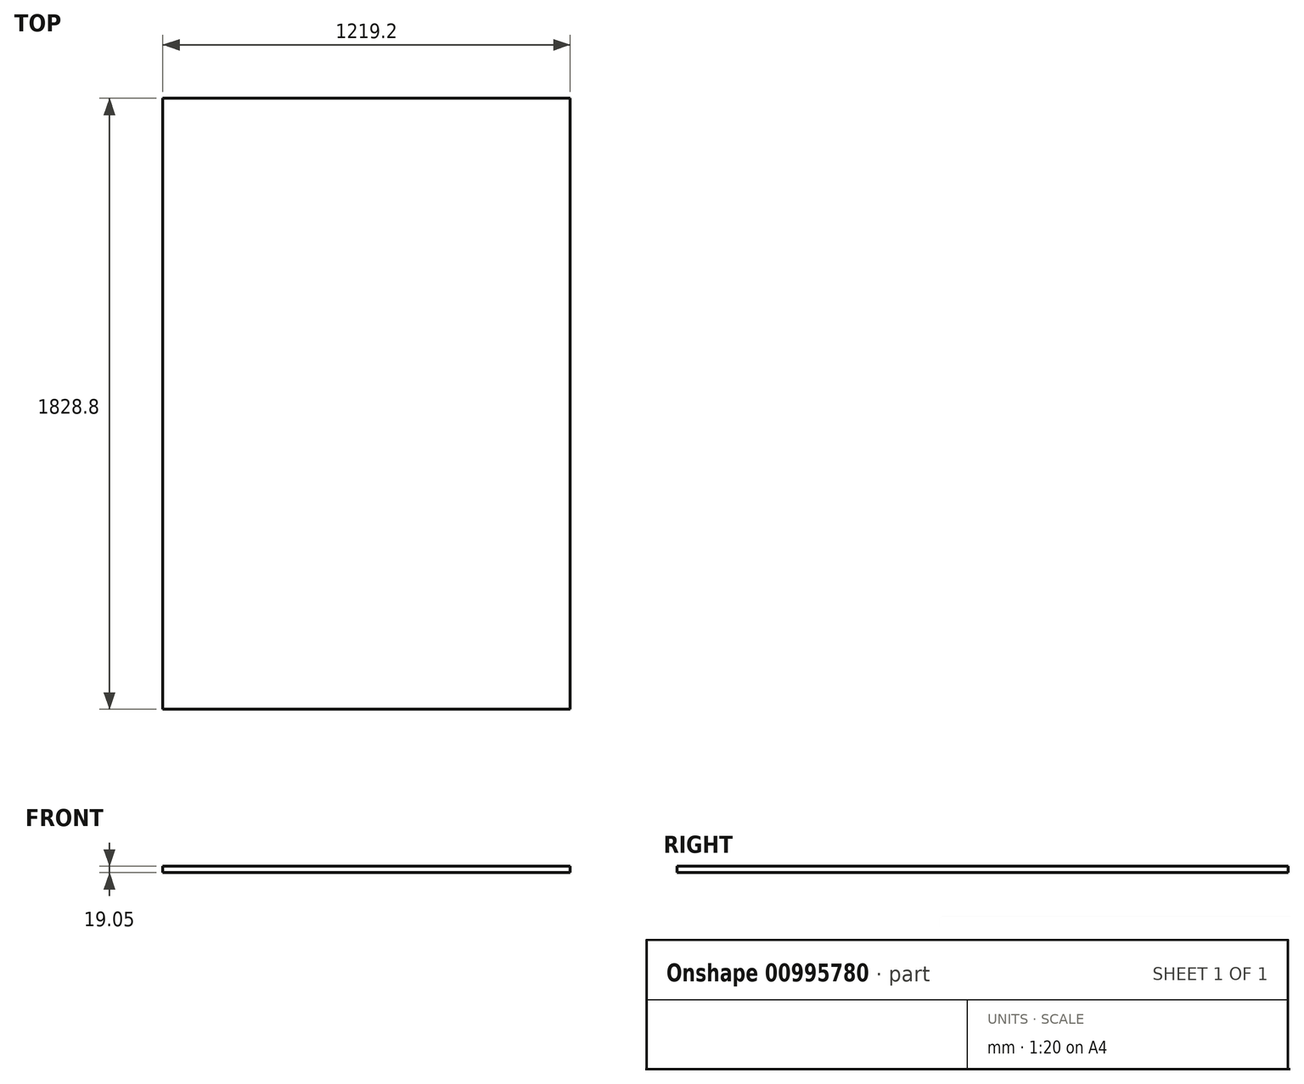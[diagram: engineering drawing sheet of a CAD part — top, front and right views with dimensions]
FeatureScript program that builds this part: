
annotation { "Feature Type Name" : "Feature", "Feature Type Description" : "" }
export const myFeature = defineFeature(function(context is Context, id is Id, definition is map)
    precondition{}
    {
        {
            var Q0;
            Q0=qCreatedBy(makeId("Top.planeOp"),FACE);
            var sketch = newSketch(context, id + "F0", { "sketchPlane" : qUnion([Q0])});
            skLineSegment(sketch, "E0.bottom", {"start": v(0, 0) * mm, "end": v(1219.2, 0) * mm});
            skLineSegment(sketch, "E0.top", {"start": v(0, 1828.8) * mm, "end": v(1219.2, 1828.8) * mm});
            skLineSegment(sketch, "E0.left", {"start": v(0, 0) * mm, "end": v(0, 1828.8) * mm});
            skLineSegment(sketch, "E0.right", {"start": v(1219.2, 0) * mm, "end": v(1219.2, 1828.8) * mm});
            skSolve(sketch);
        }
        {
            var Q0;
            Q0=makeQuery(id+"F0.imprint","IMPRINT",FACE,{"disambiguationData":[TD([[makeQuery(id+"F0.imprint","IMPRINT",EDGE,{"derivedFrom":sQuery(id+"F0.wireOp",EDGE,"E0.bottom")}),1.0]])]});
            extrude(context, id + "F1", {"entities" : qUnion([Q0]), "depth" : 19.05 * mm, "offsetDistance" : 25.4 * mm});
        }
    });
